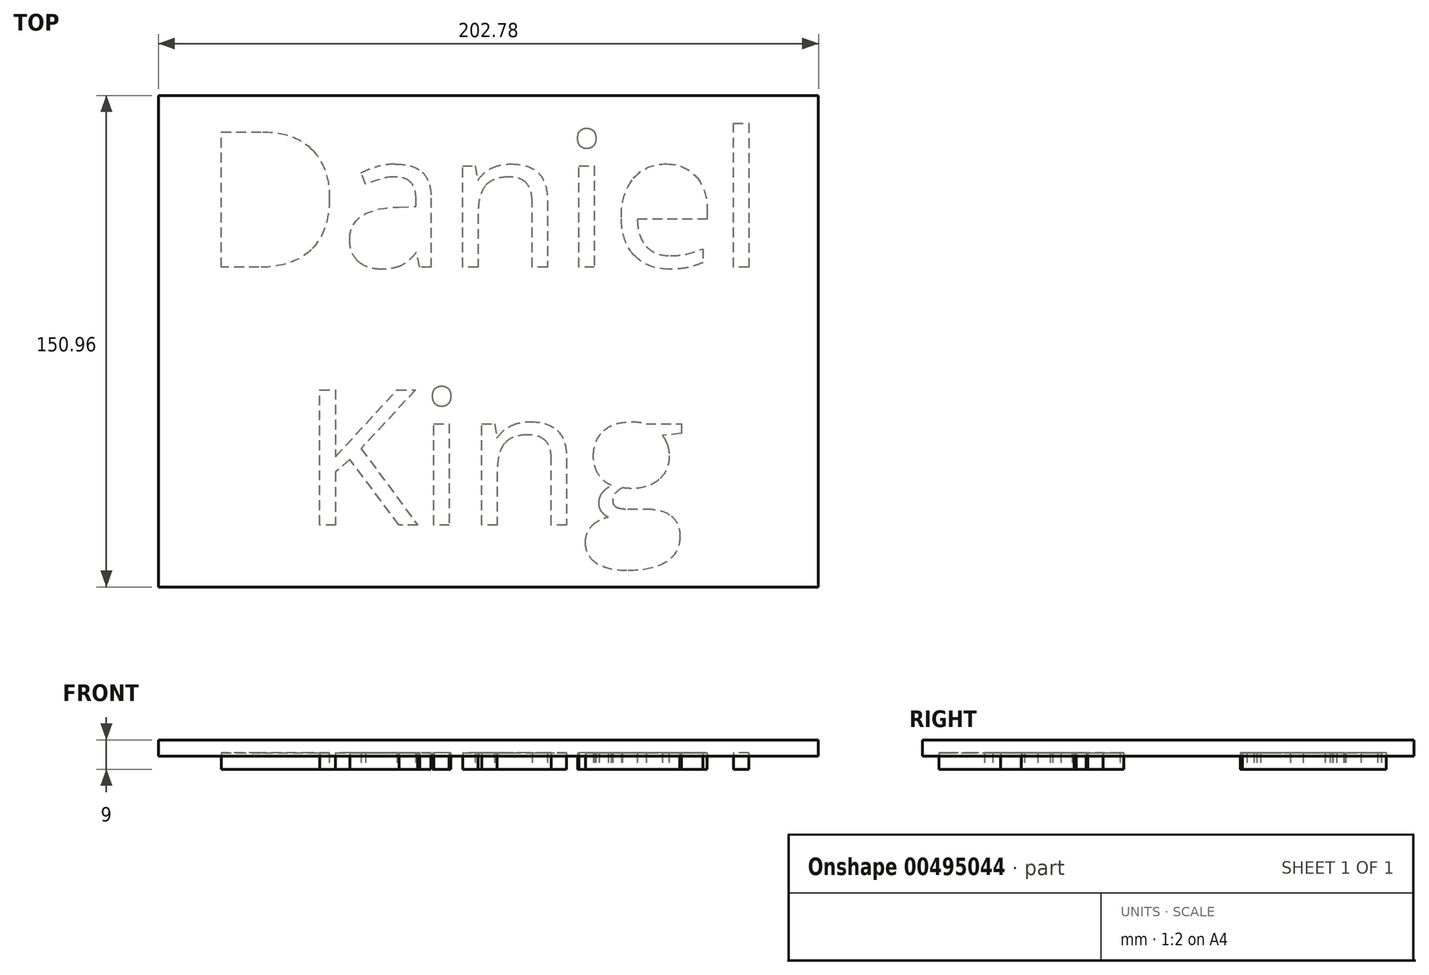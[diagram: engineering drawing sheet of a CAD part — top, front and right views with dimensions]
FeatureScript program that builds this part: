
annotation { "Feature Type Name" : "Feature", "Feature Type Description" : "" }
export const myFeature = defineFeature(function(context is Context, id is Id, definition is map)
    precondition{}
    {
        {
            var Q0;
            Q0=qCreatedBy(makeId("Top.planeOp"),FACE);
            var sketch = newSketch(context, id + "F0", { "sketchPlane" : qUnion([Q0])});
            skText(sketch, "E0", { "text": "Daniel\n  King", "fontName": "OpenSans-Regular.ttf"});
            const initialGuessF0  = {"E0": [-0.05614, -0.01336, 1, 0, 0.04193]};
            skSetInitialGuess(sketch, initialGuessF0);
            skSolve(sketch);
        }
        {
            var Q0;
            Q0 = qSketchRegion(id + "F0", true);
            var Q1;
            Q1=makeQuery(id+"F0.imprint","IMPRINT",FACE,{"disambiguationData":[TD([[makeQuery(id+"F0.imprint","IMPRINT",EDGE,{"derivedFrom":sQuery(id+"F0.wireOp",EDGE,"E0.sketch_text.stroke-70")}),-1.0]])]});
            var Q2;
            Q2=makeQuery(id+"F0.imprint","IMPRINT",FACE,{"disambiguationData":[TD([[makeQuery(id+"F0.imprint","IMPRINT",EDGE,{"derivedFrom":sQuery(id+"F0.wireOp",EDGE,"E0.sketch_text.stroke-33")}),1.0]])]});
            var Q3;
            Q3=makeQuery(id+"F0.imprint","IMPRINT",FACE,{"disambiguationData":[TD([[makeQuery(id+"F0.imprint","IMPRINT",EDGE,{"derivedFrom":sQuery(id+"F0.wireOp",EDGE,"E0.sketch_text.stroke-14")}),-1.0]])]});
            var Q4;
            Q4=makeQuery(id+"F0.imprint","IMPRINT",FACE,{"disambiguationData":[TD([[makeQuery(id+"F0.imprint","IMPRINT",EDGE,{"derivedFrom":sQuery(id+"F0.wireOp",EDGE,"E0.sketch_text.stroke-7")}),1.0]])]});
            var Q5;
            Q5=makeQuery(id+"F0.imprint","IMPRINT",FACE,{"disambiguationData":[TD([[makeQuery(id+"F0.imprint","IMPRINT",EDGE,{"derivedFrom":sQuery(id+"F0.wireOp",EDGE,"E0.sketch_text.stroke-0")}),-1.0]])]});
            var Q6;
            Q6=makeQuery(id+"F0.imprint","IMPRINT",FACE,{"disambiguationData":[TD([[makeQuery(id+"F0.imprint","IMPRINT",EDGE,{"derivedFrom":sQuery(id+"F0.wireOp",EDGE,"E0.sketch_text.stroke-117")}),-1.0]])]});
            var Q7;
            Q7=makeQuery(id+"F0.imprint","IMPRINT",FACE,{"disambiguationData":[TD([[makeQuery(id+"F0.imprint","IMPRINT",EDGE,{"derivedFrom":sQuery(id+"F0.wireOp",EDGE,"E0.sketch_text.stroke-109")}),-1.0]])]});
            var Q8;
            Q8=makeQuery(id+"F0.imprint","IMPRINT",FACE,{"disambiguationData":[TD([[makeQuery(id+"F0.imprint","IMPRINT",EDGE,{"derivedFrom":sQuery(id+"F0.wireOp",EDGE,"E0.sketch_text.stroke-105")}),-1.0]])]});
            var Q9;
            Q9=makeQuery(id+"F0.imprint","IMPRINT",FACE,{"disambiguationData":[TD([[makeQuery(id+"F0.imprint","IMPRINT",EDGE,{"derivedFrom":sQuery(id+"F0.wireOp",EDGE,"E0.sketch_text.stroke-93")}),-1.0]])]});
            var Q10;
            Q10=makeQuery(id+"F0.imprint","IMPRINT",FACE,{"disambiguationData":[TD([[makeQuery(id+"F0.imprint","IMPRINT",EDGE,{"derivedFrom":sQuery(id+"F0.wireOp",EDGE,"E0.sketch_text.stroke-89")}),-1.0]])]});
            var Q11;
            Q11=makeQuery(id+"F0.imprint","IMPRINT",FACE,{"disambiguationData":[TD([[makeQuery(id+"F0.imprint","IMPRINT",EDGE,{"derivedFrom":sQuery(id+"F0.wireOp",EDGE,"E0.sketch_text.stroke-62")}),-1.0]])]});
            var Q12;
            Q12=makeQuery(id+"F0.imprint","IMPRINT",FACE,{"disambiguationData":[TD([[makeQuery(id+"F0.imprint","IMPRINT",EDGE,{"derivedFrom":sQuery(id+"F0.wireOp",EDGE,"E0.sketch_text.stroke-58")}),-1.0]])]});
            var Q13;
            Q13=makeQuery(id+"F0.imprint","IMPRINT",FACE,{"disambiguationData":[TD([[makeQuery(id+"F0.imprint","IMPRINT",EDGE,{"derivedFrom":sQuery(id+"F0.wireOp",EDGE,"E0.sketch_text.stroke-41")}),-1.0]])]});
            var Q14;
            Q14=makeQuery(id+"F0.imprint","IMPRINT",FACE,{"disambiguationData":[TD([[makeQuery(id+"F0.imprint","IMPRINT",EDGE,{"derivedFrom":sQuery(id+"F0.wireOp",EDGE,"E0.sketch_text.stroke-163")}),1.0]])]});
            var Q15;
            Q15=makeQuery(id+"F0.imprint","IMPRINT",FACE,{"disambiguationData":[TD([[makeQuery(id+"F0.imprint","IMPRINT",EDGE,{"derivedFrom":sQuery(id+"F0.wireOp",EDGE,"E0.sketch_text.stroke-84")}),1.0]])]});
            var Q16;
            Q16=makeQuery(id+"F0.imprint","IMPRINT",FACE,{"disambiguationData":[TD([[makeQuery(id+"F0.imprint","IMPRINT",EDGE,{"derivedFrom":sQuery(id+"F0.wireOp",EDGE,"E0.sketch_text.stroke-172")}),1.0]])]});
            var Q17;
            Q17=makeQuery(id+"F0.imprint","IMPRINT",FACE,{"disambiguationData":[TD([[makeQuery(id+"F0.imprint","IMPRINT",EDGE,{"derivedFrom":sQuery(id+"F0.wireOp",EDGE,"E0.sketch_text.stroke-134")}),-1.0]])]});
            extrude(context, id + "F1", {"entities" : qUnion([Q0, Q1, Q2, Q3, Q4, Q5, Q6, Q7, Q8, Q9, Q10, Q11, Q12, Q13, Q14, Q15, Q16, Q17]), "depth" : 5 * mm});
        }
        {
            var Q0;
            Q0=qCreatedBy(makeId("Top.planeOp"),FACE);
            var sketch = newSketch(context, id + "F2", { "sketchPlane" : qUnion([Q0])});
            skLineSegment(sketch, "E1.bottom", {"start": v(-69.77, 39.37) * mm, "end": v(133, 39.37) * mm});
            skLineSegment(sketch, "E1.top", {"start": v(-69.77, -111.59) * mm, "end": v(133, -111.59) * mm});
            skLineSegment(sketch, "E1.left", {"start": v(-69.77, 39.37) * mm, "end": v(-69.77, -111.59) * mm});
            skLineSegment(sketch, "E1.right", {"start": v(133, 39.37) * mm, "end": v(133, -111.59) * mm});
            skSolve(sketch);
        }
        {
            var Q0;
            Q0=makeQuery(id+"F2.imprint","IMPRINT",FACE,{"disambiguationData":[TD([[makeQuery(id+"F2.imprint","IMPRINT",EDGE,{"derivedFrom":sQuery(id+"F2.wireOp",EDGE,"E1.bottom")}),-1.0]])]});
            extrude(context, id + "F3", {"entities" : qUnion([Q0]), "depth" : 9 * mm, "hasSecondDirection" : true, "secondDirectionOppositeDirection" : true, "secondDirectionDepth" : -4 * mm});
        }
    });
